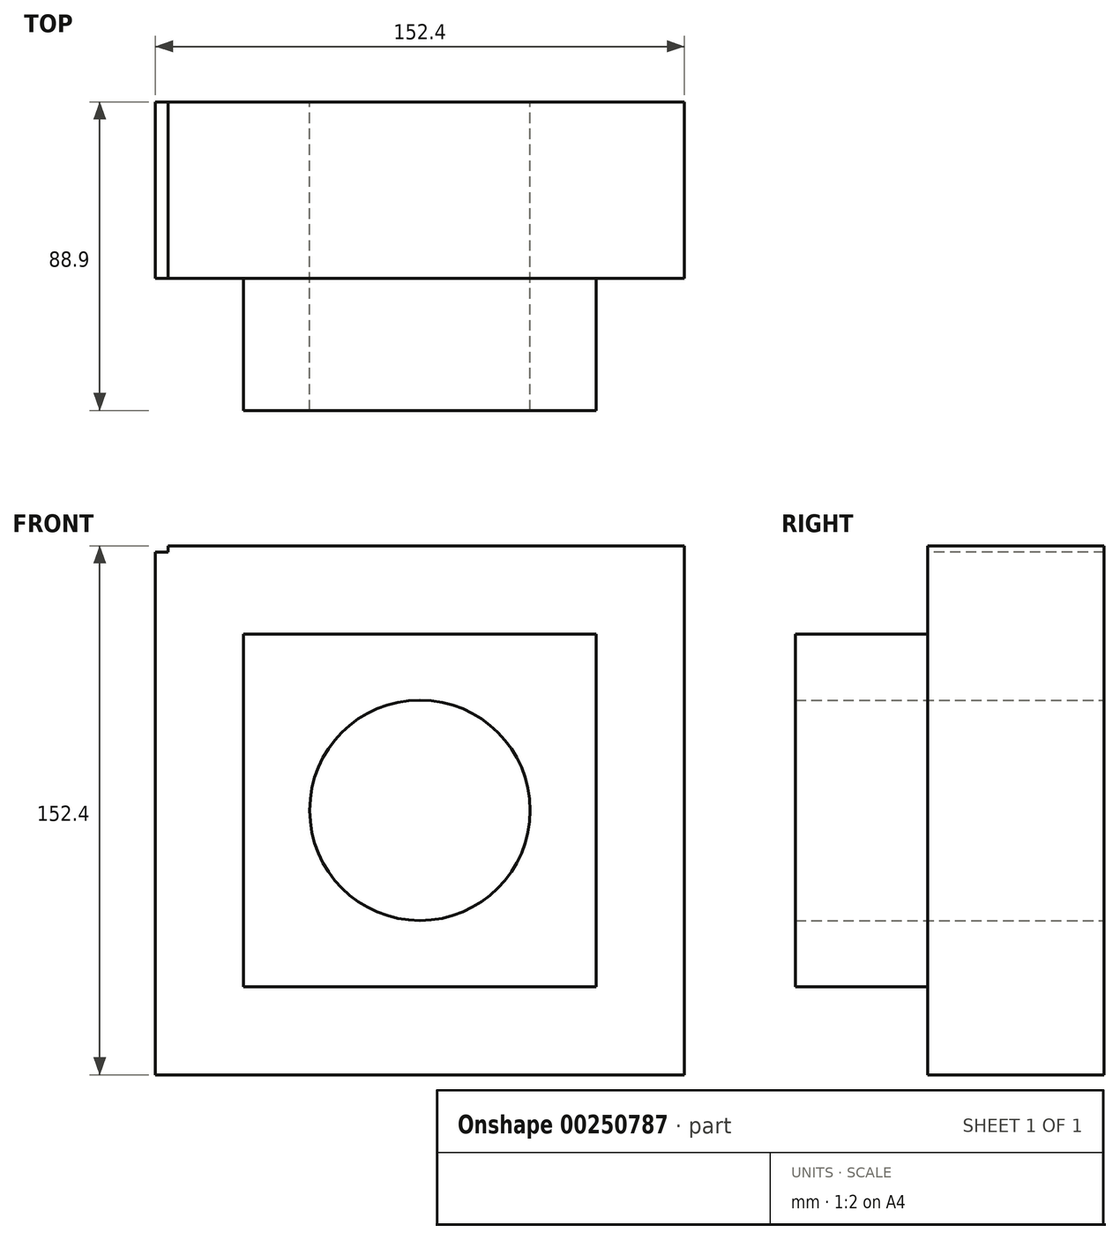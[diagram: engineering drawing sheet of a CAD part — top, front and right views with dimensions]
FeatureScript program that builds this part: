
annotation { "Feature Type Name" : "Feature", "Feature Type Description" : "" }
export const myFeature = defineFeature(function(context is Context, id is Id, definition is map)
    precondition{}
    {
        {
            var Q0;
            Q0=qCreatedBy(makeId("Front.planeOp"),FACE);
            var sketch = newSketch(context, id + "F0", { "sketchPlane" : qUnion([Q0])});
            skCircle(sketch, "E0", {"center": v(0, 0) * mm, "radius": 31.75 * mm});
            skLineSegment(sketch, "E1.bottom", {"start": v(-76.2, -76.2) * mm, "end": v(76.2, -76.2) * mm});
            skLineSegment(sketch, "E1.top", {"start": v(-76.2, 76.2) * mm, "end": v(76.2, 76.2) * mm});
            skLineSegment(sketch, "E1.left", {"start": v(-76.2, -76.2) * mm, "end": v(-76.2, 76.2) * mm});
            skLineSegment(sketch, "E1.right", {"start": v(76.2, -76.2) * mm, "end": v(76.2, 76.2) * mm});
            skLineSegment(sketch, "E2.bottom", {"start": v(-50.8, -50.8) * mm, "end": v(50.8, -50.8) * mm});
            skLineSegment(sketch, "E2.top", {"start": v(-50.8, 50.8) * mm, "end": v(50.8, 50.8) * mm});
            skLineSegment(sketch, "E2.left", {"start": v(-50.8, -50.8) * mm, "end": v(-50.8, 50.8) * mm});
            skLineSegment(sketch, "E2.right", {"start": v(50.8, -50.8) * mm, "end": v(50.8, 50.8) * mm});
            skSolve(sketch);
        }
        {
            var Q0;
            Q0=makeQuery(id+"F0.imprint","IMPRINT",FACE,{"disambiguationData":[TD([[makeQuery(id+"F0.imprint","IMPRINT",EDGE,{"derivedFrom":sQuery(id+"F0.wireOp",EDGE,"E0")}),-1.0]])]});
            extrude(context, id + "F1", {"entities" : qUnion([Q0]), "depth" : 38.1 * mm});
        }
        {
            var Q0;
            Q0=qCreatedBy(makeId("Front.planeOp"),FACE);
            var sketch = newSketch(context, id + "F2", { "sketchPlane" : qUnion([Q0])});
            skLineSegment(sketch, "E3.bottom", {"start": v(-72.54, 74.36) * mm, "end": v(-79.23, 74.36) * mm});
            skLineSegment(sketch, "E3.top", {"start": v(-72.54, 77.5) * mm, "end": v(-79.23, 77.5) * mm});
            skLineSegment(sketch, "E3.left", {"start": v(-72.54, 74.36) * mm, "end": v(-72.54, 77.5) * mm});
            skLineSegment(sketch, "E3.right", {"start": v(-79.23, 74.36) * mm, "end": v(-79.23, 77.5) * mm});
            skPoint(sketch, "E3.middle", {"position": v(-75.89, 75.93) * mm});
            skLineSegment(sketch, "E4.bottom", {"start": v(76.2, 76.2) * mm, "end": v(-76.2, 76.2) * mm});
            skLineSegment(sketch, "E4.top", {"start": v(76.2, -76.2) * mm, "end": v(-76.2, -76.2) * mm});
            skLineSegment(sketch, "E4.left", {"start": v(76.2, 76.2) * mm, "end": v(76.2, -76.2) * mm});
            skLineSegment(sketch, "E4.right", {"start": v(-76.2, 76.2) * mm, "end": v(-76.2, -76.2) * mm});
            skPoint(sketch, "E4.middle", {"position": v(0, 0) * mm});
            skCircle(sketch, "E5", {"center": v(0, 0) * mm, "radius": 31.75 * mm});
            skSolve(sketch);
        }
        {
            var Q0;
            {var subQ4=sQuery(id+"F2.wireOp",EDGE,"E4.top");Q0=makeQuery(id+"F2.imprint","IMPRINT",FACE,{"disambiguationData":[TD([[makeQuery(id+"F2.imprint","IMPRINT",EDGE,{"derivedFrom":subQ4}),-1.0]])]});}
            extrude(context, id + "F3", {"entities" : qUnion([Q0]), "operationType" : NewBodyOperationType.ADD, "oppositeDirection" : true, "depth" : 50.8 * mm});
        }
    });
